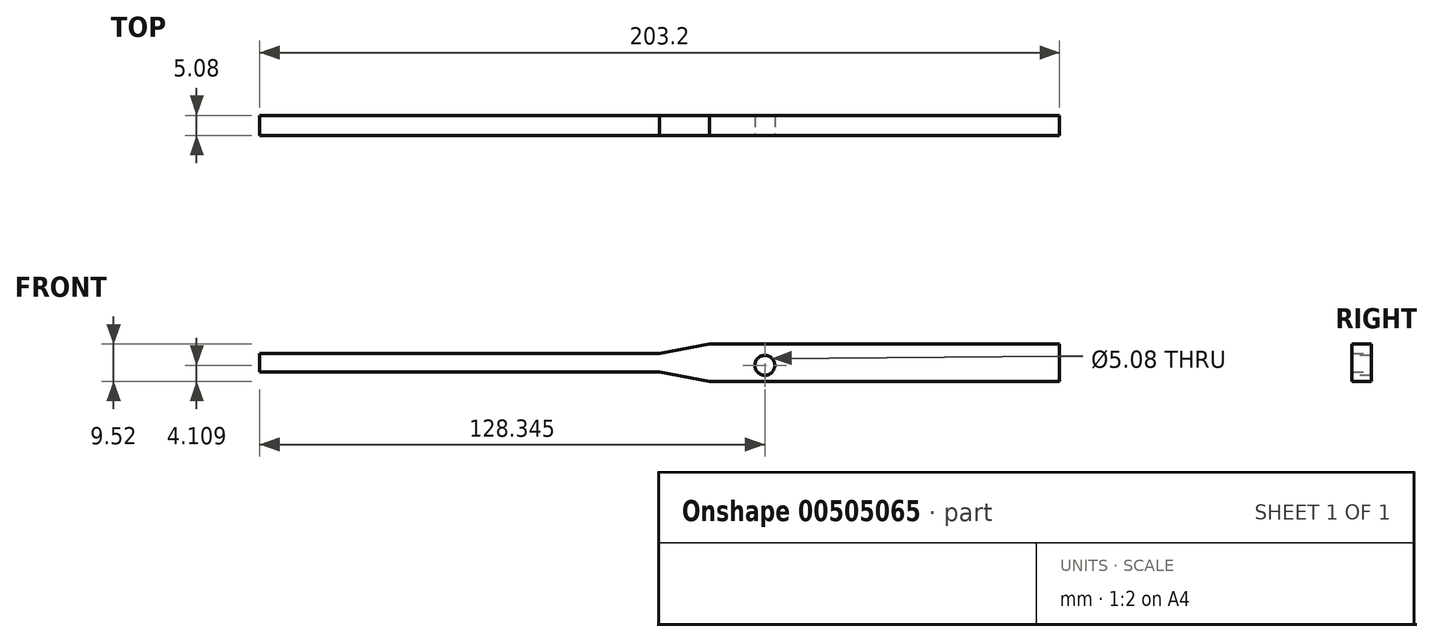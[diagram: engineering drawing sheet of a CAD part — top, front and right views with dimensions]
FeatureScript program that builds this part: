
annotation { "Feature Type Name" : "Feature", "Feature Type Description" : "" }
export const myFeature = defineFeature(function(context is Context, id is Id, definition is map)
    precondition{}
    {
        {
            var Q0;
            Q0=qCreatedBy(makeId("Front.planeOp"),FACE);
            var sketch = newSketch(context, id + "F0", { "sketchPlane" : qUnion([Q0])});
            skLineSegment(sketch, "E0", {"start": v(101.6, 4.76) * mm, "end": v(12.7, 4.76) * mm});
            skLineSegment(sketch, "E1", {"start": v(12.7, 4.76) * mm, "end": v(0, 2.37) * mm});
            skLineSegment(sketch, "E2", {"start": v(0, 2.37) * mm, "end": v(-101.6, 2.37) * mm});
            skLineSegment(sketch, "E3", {"start": v(-101.6, 2.37) * mm, "end": v(-101.6, 0) * mm});
            skLineSegment(sketch, "E4", {"start": v(101.6, 4.76) * mm, "end": v(101.6, 0) * mm});
            skLineSegment(sketch, "E5.MirrorCS", {"start": v(-101.6, -2.37) * mm, "end": v(-101.6, 0) * mm});
            skLineSegment(sketch, "E6.MirrorCS", {"start": v(101.6, -4.76) * mm, "end": v(101.6, 0) * mm});
            skLineSegment(sketch, "E7.MirrorCS", {"start": v(101.6, -4.76) * mm, "end": v(12.7, -4.76) * mm});
            skLineSegment(sketch, "E8.MirrorCS", {"start": v(0, -2.37) * mm, "end": v(-101.6, -2.37) * mm});
            skLineSegment(sketch, "E9.MirrorCS", {"start": v(12.7, -4.76) * mm, "end": v(0, -2.37) * mm});
            skSolve(sketch);
        }
        {
            var Q0;
            Q0=makeQuery(id+"F0.imprint","IMPRINT",FACE,{"disambiguationData":[TD([[makeQuery(id+"F0.imprint","IMPRINT",EDGE,{"derivedFrom":sQuery(id+"F0.wireOp",EDGE,"E0")}),1.0]])]});
            extrude(context, id + "F1", {"entities" : qUnion([Q0]), "depth" : 5.08 * mm});
        }
        {
            var Q0;
            Q0=makeQuery(id+"F1.opExtrude","CAP_FACE",FACE,{"disambiguationData":[OSD([sQuery(id+"F0.wireOp",EDGE,"E0"),sQuery(id+"F0.wireOp",EDGE,"E1"),sQuery(id+"F0.wireOp",EDGE,"E2"),sQuery(id+"F0.wireOp",EDGE,"E3"),sQuery(id+"F0.wireOp",EDGE,"E4"),sQuery(id+"F0.wireOp",EDGE,"E5.MirrorCS"),sQuery(id+"F0.wireOp",EDGE,"E6.MirrorCS"),sQuery(id+"F0.wireOp",EDGE,"E7.MirrorCS"),sQuery(id+"F0.wireOp",EDGE,"E8.MirrorCS"),sQuery(id+"F0.wireOp",EDGE,"E9.MirrorCS")])],"isStart":false});
            var sketch = newSketch(context, id + "F2", { "sketchPlane" : qUnion([Q0])});
            skCircle(sketch, "E10", {"center": v(26.75, -0.65) * mm, "radius": 2.54 * mm});
            skSolve(sketch);
        }
        {
            var Q0;
            Q0 = qSketchRegion(id + "F2", true);
            extrude(context, id + "F3", {"entities" : qUnion([Q0]), "operationType" : NewBodyOperationType.REMOVE, "oppositeDirection" : true, "depth" : 25.4 * mm});
        }
    });
